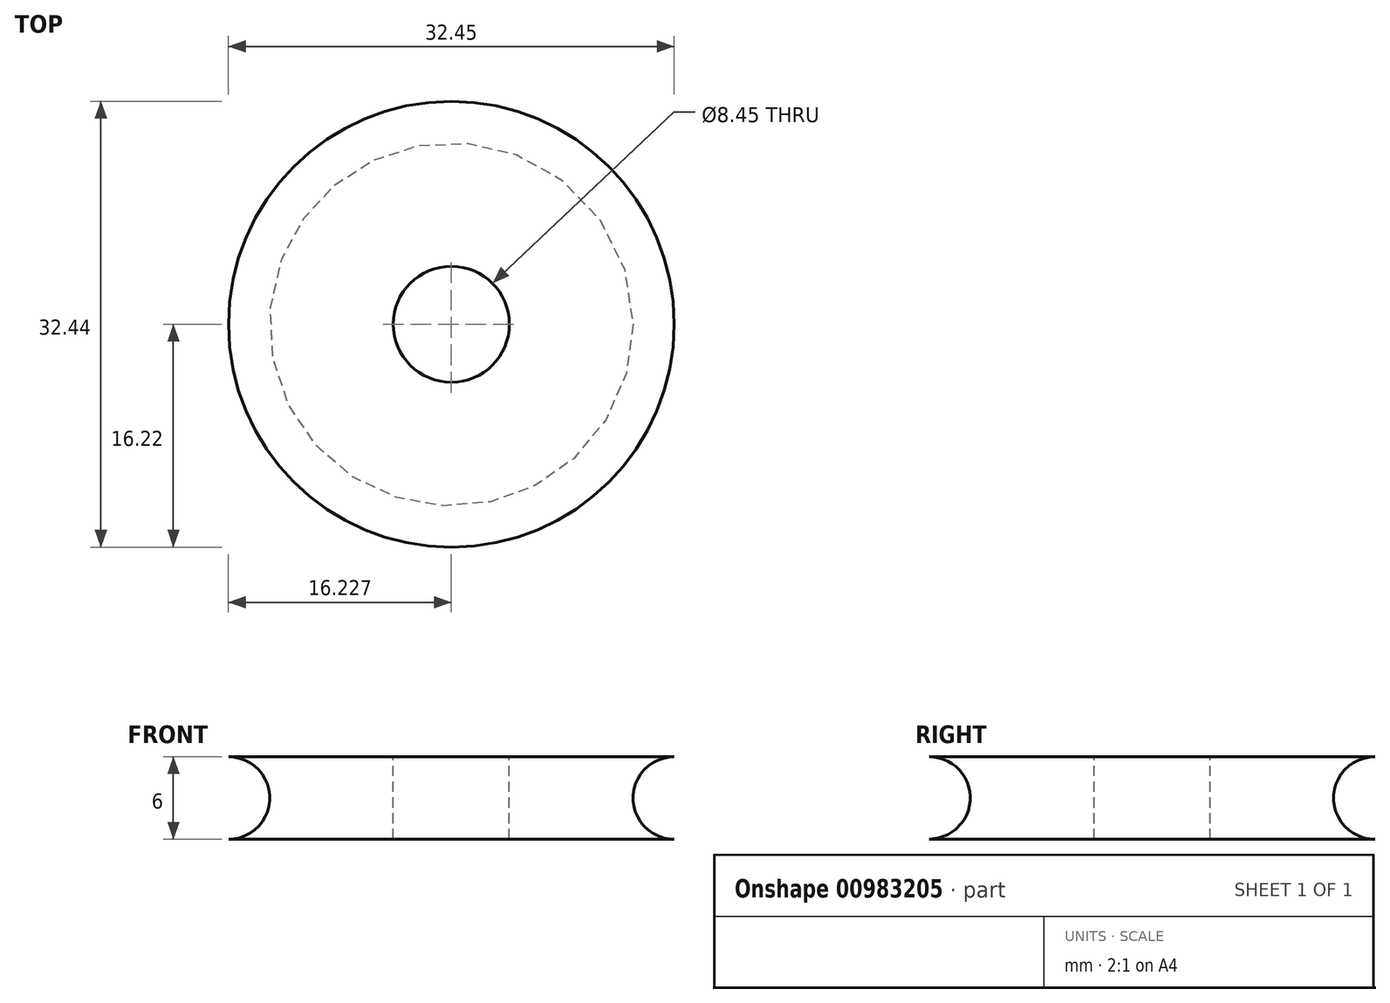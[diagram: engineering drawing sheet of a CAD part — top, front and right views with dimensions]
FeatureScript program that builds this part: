
annotation { "Feature Type Name" : "Feature", "Feature Type Description" : "" }
export const myFeature = defineFeature(function(context is Context, id is Id, definition is map)
    precondition{}
    {
        {
            var Q0;
            Q0=qCreatedBy(makeId("Front.planeOp"),FACE);
            var sketch = newSketch(context, id + "F0", { "sketchPlane" : qUnion([Q0])});
            skLineSegment(sketch, "E0.bottom", {"start": v(1.66, 0) * mm, "end": v(13.66, 0) * mm});
            skLineSegment(sketch, "E0.top", {"start": v(1.66, 6) * mm, "end": v(13.66, 6) * mm});
            skLineSegment(sketch, "E0.left", {"start": v(1.66, 0) * mm, "end": v(1.66, 6) * mm});
            skLineSegment(sketch, "E0.right", {"start": v(13.66, 0) * mm, "end": v(13.66, 6) * mm});
            skLineSegment(sketch, "E1.top", {"start": v(1.66, 7.5) * mm, "end": v(13.66, 7.5) * mm});
            skLineSegment(sketch, "E1.left", {"start": v(1.66, 6) * mm, "end": v(1.66, 7.5) * mm});
            skLineSegment(sketch, "E1.right", {"start": v(13.66, 6) * mm, "end": v(13.66, 7.5) * mm});
            skLineSegment(sketch, "E2.top", {"start": v(1.66, -1.5) * mm, "end": v(13.66, -1.5) * mm});
            skLineSegment(sketch, "E2.left", {"start": v(1.66, 0) * mm, "end": v(1.66, -1.5) * mm});
            skLineSegment(sketch, "E2.right", {"start": v(13.66, 0) * mm, "end": v(13.66, -1.5) * mm});
            skArc(sketch, "E3", {"start": v(1.66, 0) * mm, "mid": v(4.66, 3) * mm, "end": v(1.66, 6) * mm});
            skLineSegment(sketch, "E4", {"start": v(17.89, 10.54) * mm, "end": v(17.89, -3.21) * mm, "construction": true});
            skSolve(sketch);
        }
        {
            var Q0;
            Q0=makeQuery(id+"F0.imprint","IMPRINT",FACE,{"disambiguationData":[TD([[makeQuery(id+"F0.imprint","IMPRINT",EDGE,{"derivedFrom":sQuery(id+"F0.wireOp",EDGE,"E0.top")}),1.0]])]});
            var Q1;
            Q1=makeQuery(id+"F0.imprint","IMPRINT",FACE,{"disambiguationData":[TD([[makeQuery(id+"F0.imprint","IMPRINT",EDGE,{"derivedFrom":sQuery(id+"F0.wireOp",EDGE,"E0.right")}),1.0]])]});
            var Q2;
            Q2=makeQuery(id+"F0.imprint","IMPRINT",FACE,{"disambiguationData":[TD([[makeQuery(id+"F0.imprint","IMPRINT",EDGE,{"derivedFrom":sQuery(id+"F0.wireOp",EDGE,"E0.bottom")}),-1.0]])]});
            var Q3;
            Q3=sQuery(id+"F0.wireOp",EDGE,"E4");
            revolve(context, id + "F1", {"surfaceOperationType" : NewSurfaceOperationType.NEW, "entities" : qUnion([Q0, Q1, Q2]), "axis" : qUnion([Q3]), "revolveType" : RevolveType.FULL});
        }
    });
